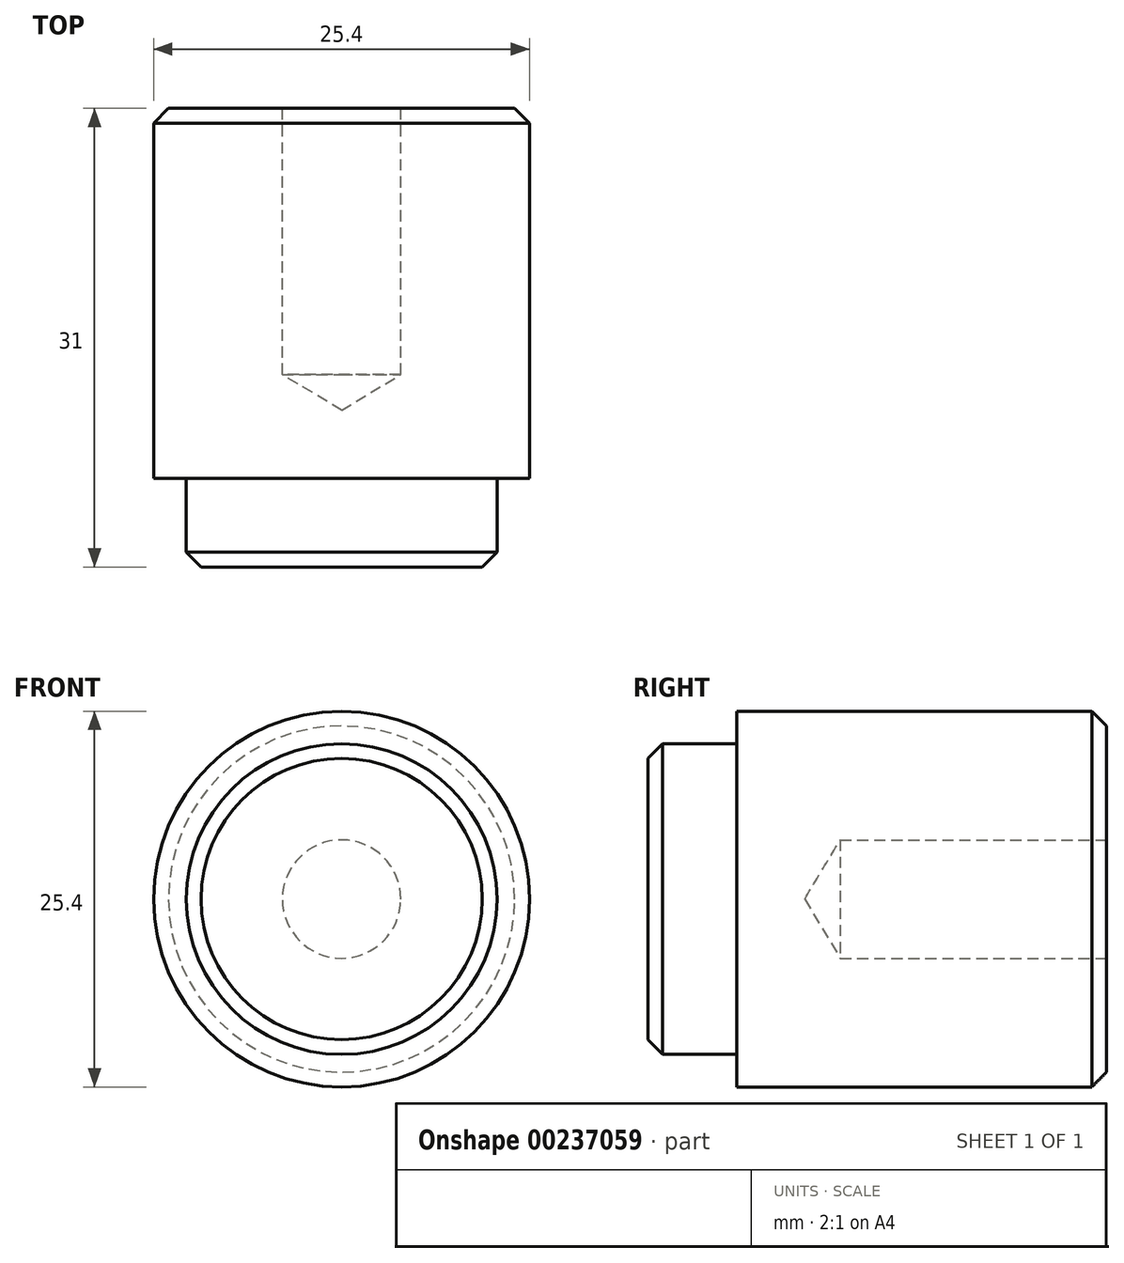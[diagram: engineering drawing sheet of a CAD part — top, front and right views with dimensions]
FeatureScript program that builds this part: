
annotation { "Feature Type Name" : "Feature", "Feature Type Description" : "" }
export const myFeature = defineFeature(function(context is Context, id is Id, definition is map)
    precondition{}
    {
        {
            var Q0;
            Q0=qCreatedBy(makeId("Front.planeOp"),FACE);
            var sketch = newSketch(context, id + "F0", { "sketchPlane" : qUnion([Q0])});
            skCircle(sketch, "E0", {"center": v(0, 0) * mm, "radius": 12.7 * mm});
            skSolve(sketch);
        }
        {
            var Q0;
            Q0=makeQuery(id+"F0.imprint","IMPRINT",FACE,{"disambiguationData":[TD([[makeQuery(id+"F0.imprint","IMPRINT",EDGE,{"derivedFrom":sQuery(id+"F0.wireOp",EDGE,"E0")}),1.0]])]});
            extrude(context, id + "F1", {"entities" : qUnion([Q0]), "depth" : 25 * mm});
        }
        {
            var Q0;
            Q0=makeQuery(id+"F1.opExtrude","CAP_FACE",FACE,{"disambiguationData":[OSD([sQuery(id+"F0.wireOp",EDGE,"E0")])],"isStart":false});
            var sketch = newSketch(context, id + "F2", { "sketchPlane" : qUnion([Q0])});
            skCircle(sketch, "E1", {"center": v(0, 0) * mm, "radius": 10.5 * mm});
            skSolve(sketch);
        }
        {
            var Q0;
            Q0=makeQuery(id+"F2.imprint","IMPRINT",FACE,{"disambiguationData":[TD([[makeQuery(id+"F2.imprint","IMPRINT",EDGE,{"derivedFrom":sQuery(id+"F2.wireOp",EDGE,"E1")}),1.0]])]});
            extrude(context, id + "F3", {"entities" : qUnion([Q0]), "operationType" : NewBodyOperationType.ADD, "depth" : 6 * mm});
        }
        {
            var Q0;
            Q0=makeQuery(id+"F3.opExtrude","CAP_EDGE",EDGE,{"disambiguationData":[OSD([sQuery(id+"F2.wireOp",EDGE,"E1")])],"isStart":false});
            var Q1;
            Q1=makeQuery(id+"F1.opExtrude","CAP_EDGE",EDGE,{"disambiguationData":[OSD([sQuery(id+"F0.wireOp",EDGE,"E0")])],"isStart":true});
            chamfer(context, id + "F4", {"entities" : qUnion([Q0, Q1]), "width" : 1 * mm, "tangentPropagation" : true});
        }
        {
            var Q0;
            Q0=makeQuery(id+"F1.opExtrude","CAP_FACE",FACE,{"disambiguationData":[OSD([sQuery(id+"F0.wireOp",EDGE,"E0")])],"isStart":true});
            var sketch = newSketch(context, id + "F5", { "sketchPlane" : qUnion([Q0])});
            skPoint(sketch, "E2", {"position": v(0, 0) * mm});
            skSolve(sketch);
        }
        {
            var Q0;
            Q0=sQuery(id+"F5.wireOp",VERTEX,"E2");
            var Q1;
            Q1=makeQuery(id+"F1.opExtrude","SWEPT_BODY",BODY,{"disambiguationData":[OSD([sQuery(id+"F0.wireOp",EDGE,"E0")])]});
            hole(context, id + "F6", {"style" : HoleStyle.SIMPLE, "endStyle" : HoleEndStyle.BLIND, "holeDiameter" : 8 * mm, "holeDepth" : 18 * mm, "locations" : qUnion([Q0]), "scope" : qUnion([Q1])});
        }
    });
